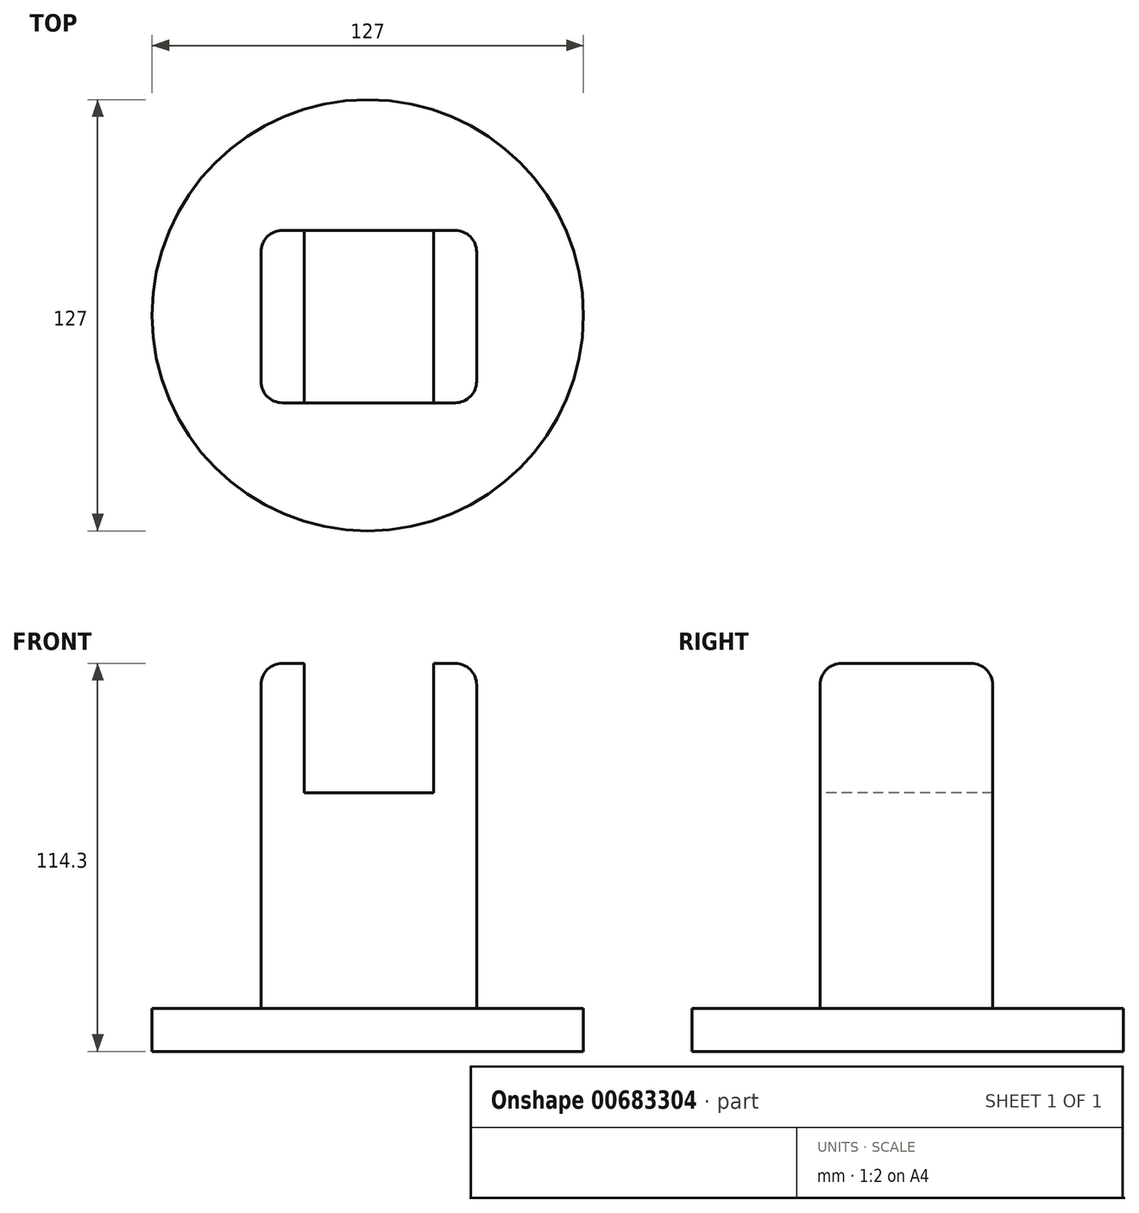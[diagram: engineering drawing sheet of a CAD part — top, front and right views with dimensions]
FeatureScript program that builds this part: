
annotation { "Feature Type Name" : "Feature", "Feature Type Description" : "" }
export const myFeature = defineFeature(function(context is Context, id is Id, definition is map)
    precondition{}
    {
        {
            var Q0;
            Q0=qCreatedBy(makeId("Top.planeOp"),FACE);
            var sketch = newSketch(context, id + "F0", { "sketchPlane" : qUnion([Q0])});
            skLineSegment(sketch, "E0.bottom", {"start": v(-125.08, 16.31) * mm, "end": v(-74.28, 16.31) * mm});
            skLineSegment(sketch, "E0.top", {"start": v(-125.08, -34.49) * mm, "end": v(-74.28, -34.49) * mm});
            skLineSegment(sketch, "E0.left", {"start": v(-131.43, 9.96) * mm, "end": v(-131.43, -28.14) * mm});
            skLineSegment(sketch, "E0.right", {"start": v(-67.93, 9.96) * mm, "end": v(-67.93, -28.14) * mm});
            skPoint(sketch, "E1.visualSharp", {"position": v(-131.43, -34.49) * mm});
            skArc(sketch, "E1.filletArc", {"start": v(-131.43, -28.14) * mm, "mid": v(-129.57, -32.63) * mm, "end": v(-125.08, -34.49) * mm});
            skPoint(sketch, "E2.visualSharp", {"position": v(-131.43, 16.31) * mm});
            skArc(sketch, "E2.filletArc", {"start": v(-125.08, 16.31) * mm, "mid": v(-129.57, 14.45) * mm, "end": v(-131.43, 9.96) * mm});
            skPoint(sketch, "E3.visualSharp", {"position": v(-67.93, -34.49) * mm});
            skArc(sketch, "E3.filletArc", {"start": v(-74.28, -34.49) * mm, "mid": v(-69.79, -32.63) * mm, "end": v(-67.93, -28.14) * mm});
            skPoint(sketch, "E4.visualSharp", {"position": v(-67.93, 16.31) * mm});
            skArc(sketch, "E4.filletArc", {"start": v(-67.93, 9.96) * mm, "mid": v(-69.79, 14.45) * mm, "end": v(-74.28, 16.31) * mm});
            skSolve(sketch);
        }
        {
            var Q0;
            Q0=makeQuery(id+"F0.imprint","IMPRINT",FACE,{"disambiguationData":[TD([[makeQuery(id+"F0.imprint","IMPRINT",EDGE,{"derivedFrom":sQuery(id+"F0.wireOp",EDGE,"E0.bottom")}),-1.0]])]});
            extrude(context, id + "F1", {"entities" : qUnion([Q0]), "depth" : 76.2 * mm, "offsetDistance" : 25.4 * mm});
        }
        {
            var Q0;
            Q0=qCreatedBy(makeId("Top.planeOp"),FACE);
            var sketch = newSketch(context, id + "F2", { "sketchPlane" : qUnion([Q0])});
            skCircle(sketch, "E5", {"center": v(-99.98, -8.68) * mm, "radius": 63.5 * mm});
            skSolve(sketch);
        }
        {
            var Q0;
            Q0=makeQuery(id+"F2.imprint","IMPRINT",FACE,{"disambiguationData":[TD([[makeQuery(id+"F2.imprint","IMPRINT",EDGE,{"derivedFrom":sQuery(id+"F2.wireOp",EDGE,"E5")}),1.0]])]});
            extrude(context, id + "F3", {"entities" : qUnion([Q0]), "operationType" : NewBodyOperationType.ADD, "depth" : 12.7 * mm, "offsetDistance" : 25.4 * mm});
        }
        {
            var Q0;
            Q0=makeQuery(id+"F1.opExtrude","CAP_FACE",FACE,{"disambiguationData":[OSD([sQuery(id+"F0.wireOp",EDGE,"E0.bottom"),sQuery(id+"F0.wireOp",EDGE,"E0.top"),sQuery(id+"F0.wireOp",EDGE,"E0.left"),sQuery(id+"F0.wireOp",EDGE,"E0.right"),sQuery(id+"F0.wireOp",EDGE,"E1.filletArc"),sQuery(id+"F0.wireOp",EDGE,"E2.filletArc"),sQuery(id+"F0.wireOp",EDGE,"E3.filletArc"),sQuery(id+"F0.wireOp",EDGE,"E4.filletArc")])],"isStart":false});
            var sketch = newSketch(context, id + "F4", { "sketchPlane" : qUnion([Q0])});
            skSolve(sketch);
        }
        {
            var Q0;
            Q0=makeQuery(id+"F1.opExtrude","SWEPT_FACE",FACE,{"disambiguationData":[OSD([sQuery(id+"F0.wireOp",EDGE,"E0.left")])]});
            var sketch = newSketch(context, id + "F5", { "sketchPlane" : qUnion([Q0])});
            skLineSegment(sketch, "E6.bottom", {"start": v(-9.96, 76.2) * mm, "end": v(28.14, 76.2) * mm});
            skLineSegment(sketch, "E6.top", {"start": v(-9.96, 114.3) * mm, "end": v(28.14, 114.3) * mm});
            skLineSegment(sketch, "E6.left", {"start": v(-9.96, 76.2) * mm, "end": v(-9.96, 114.3) * mm});
            skLineSegment(sketch, "E6.right", {"start": v(28.14, 76.2) * mm, "end": v(28.14, 114.3) * mm});
            skPoint(sketch, "E7.oppositeSnap0", {"position": v(-9.96, 95.25) * mm});
            skLineSegment(sketch, "E7.left", {"start": v(-9.96, 95.25) * mm, "end": v(-9.96, 95.25) * mm});
            skSolve(sketch);
        }
        {
            var Q0;
            Q0 = qSketchRegion(id + "F4", true);
            var Q1;
            Q1=makeQuery(id+"F5.imprint","IMPRINT",FACE,{"disambiguationData":[TD([[makeQuery(id+"F5.imprint","IMPRINT",EDGE,{"derivedFrom":sQuery(id+"F5.wireOp",EDGE,"E6.bottom")}),1.0]])]});
            var Q2;
            Q2=makeQuery(id+"F5.imprint","IMPRINT",FACE,{"disambiguationData":[TD([[makeQuery(id+"F5.imprint","IMPRINT",EDGE,{"derivedFrom":sQuery(id+"F5.wireOp",EDGE,"E6.bottom")}),-1.0]])]});
            extrude(context, id + "F6", {"entities" : qUnion([Q0, Q1, Q2]), "operationType" : NewBodyOperationType.ADD, "oppositeDirection" : true, "depth" : 12.7 * mm, "offsetDistance" : 25.4 * mm});
        }
        {
            var Q0;
            Q0=makeQuery(id+"F6.opExtrude","SWEPT_FACE",FACE,{"disambiguationData":[OSD([sQuery(id+"F5.wireOp",EDGE,"E6.left")])]});
            extrude(context, id + "F7", {"entities" : qUnion([Q0]), "operationType" : NewBodyOperationType.ADD, "depth" : 6.35 * mm, "offsetDistance" : 25.4 * mm});
        }
        {
            var Q0;
            Q0=makeQuery(id+"F6.opExtrude","SWEPT_FACE",FACE,{"disambiguationData":[OSD([sQuery(id+"F5.wireOp",EDGE,"E6.right")])]});
            extrude(context, id + "F8", {"entities" : qUnion([Q0]), "operationType" : NewBodyOperationType.ADD, "depth" : 6.35 * mm, "offsetDistance" : 25.4 * mm});
        }
        {
            var Q0;
            {var subQ0=sQuery(id+"F5.wireOp",EDGE,"E6.right");Q0=makeQuery(id+"F8.opExtrude","CAP_EDGE",EDGE,{"disambiguationData":[OSD([subQ0]),TDD([makeQuery(id+"F6.opExtrude","CAP_EDGE",EDGE,{"disambiguationData":[OSD([subQ0])],"isStart":true})])],"isStart":false});}
            var Q1;
            {var subQ0=sQuery(id+"F5.wireOp",EDGE,"E6.left");Q1=makeQuery(id+"F7.opExtrude","CAP_EDGE",EDGE,{"disambiguationData":[OSD([subQ0]),TDD([makeQuery(id+"F6.opExtrude","CAP_EDGE",EDGE,{"disambiguationData":[OSD([subQ0])],"isStart":true})])],"isStart":false});}
            fillet(context, id + "F9", {"entities" : qUnion([Q0, Q1]), "radius" : 6.35 * mm, "tangentPropagation" : true, "allowEdgeOverflow" : false});
        }
        {
            var Q0;
            Q0=makeQuery(id+"F1.opExtrude","SWEPT_FACE",FACE,{"disambiguationData":[OSD([sQuery(id+"F0.wireOp",EDGE,"E0.right")])]});
            var sketch = newSketch(context, id + "F10", { "sketchPlane" : qUnion([Q0])});
            skLineSegment(sketch, "E8.bottom", {"start": v(-28.14, 76.2) * mm, "end": v(9.96, 76.2) * mm});
            skLineSegment(sketch, "E8.top", {"start": v(-28.14, 114.3) * mm, "end": v(9.96, 114.3) * mm});
            skLineSegment(sketch, "E8.left", {"start": v(-28.14, 76.2) * mm, "end": v(-28.14, 114.3) * mm});
            skLineSegment(sketch, "E8.right", {"start": v(9.96, 76.2) * mm, "end": v(9.96, 114.3) * mm});
            skSolve(sketch);
        }
        {
            var Q0;
            Q0=makeQuery(id+"F10.imprint","IMPRINT",FACE,{"disambiguationData":[TD([[makeQuery(id+"F10.imprint","IMPRINT",EDGE,{"derivedFrom":sQuery(id+"F10.wireOp",EDGE,"E8.bottom")}),-1.0]])]});
            extrude(context, id + "F11", {"entities" : qUnion([Q0]), "operationType" : NewBodyOperationType.ADD, "oppositeDirection" : true, "depth" : 12.7 * mm, "offsetDistance" : 25.4 * mm});
        }
        {
            var Q0;
            Q0=makeQuery(id+"F11.opExtrude","SWEPT_FACE",FACE,{"disambiguationData":[OSD([sQuery(id+"F10.wireOp",EDGE,"E8.right")])]});
            extrude(context, id + "F12", {"entities" : qUnion([Q0]), "operationType" : NewBodyOperationType.ADD, "depth" : 6.35 * mm, "offsetDistance" : 25.4 * mm});
        }
        {
            var Q0;
            Q0=makeQuery(id+"F11.opExtrude","SWEPT_FACE",FACE,{"disambiguationData":[OSD([sQuery(id+"F10.wireOp",EDGE,"E8.left")])]});
            extrude(context, id + "F13", {"entities" : qUnion([Q0]), "operationType" : NewBodyOperationType.ADD, "depth" : 6.35 * mm, "offsetDistance" : 25.4 * mm});
        }
        {
            var Q0;
            {var subQ0=sQuery(id+"F5.wireOp",EDGE,"E6.right");var subQ1=sQuery(id+"F0.wireOp",EDGE,"E1.filletArc");var subQ2=sQuery(id+"F0.wireOp",EDGE,"E0.left");Q0=makeQuery(id+"F8.opExtrude","CAP_EDGE",EDGE,{"disambiguationData":[OSD([subQ2,subQ1,subQ0]),TDD([makeQuery(id+"F6.opExtrude","CAP_EDGE",EDGE,{"disambiguationData":[OSD([subQ2,subQ1,subQ0])],"isStart":true})])],"isStart":false});}
            var Q1;
            {var subQ0=sQuery(id+"F10.wireOp",EDGE,"E8.left");Q1=makeQuery(id+"F13.opExtrude","CAP_EDGE",EDGE,{"disambiguationData":[OSD([subQ0]),TDD([makeQuery(id+"F11.opExtrude","CAP_EDGE",EDGE,{"disambiguationData":[OSD([subQ0])],"isStart":true})])],"isStart":false});}
            var Q2;
            {var subQ0=sQuery(id+"F10.wireOp",EDGE,"E8.right");Q2=makeQuery(id+"F12.opExtrude","CAP_EDGE",EDGE,{"disambiguationData":[OSD([subQ0]),TDD([makeQuery(id+"F11.opExtrude","CAP_EDGE",EDGE,{"disambiguationData":[OSD([subQ0])],"isStart":true})])],"isStart":false});}
            var Q3;
            {var subQ0=sQuery(id+"F10.wireOp",EDGE,"E8.left");var subQ1=sQuery(id+"F10.wireOp",EDGE,"E8.top");var subQ2=sQuery(id+"F10.wireOp",EDGE,"E8.right");Q3=makeQuery(id+"F13.boolean.opBoolean","MERGE",EDGE,{"derivedFrom":[makeQuery(id+"F12.boolean.opBoolean","MERGE",EDGE,{"derivedFrom":[makeQuery(id+"F11.opExtrude","CAP_EDGE",EDGE,{"disambiguationData":[OSD([subQ1])],"isStart":true}),makeQuery(id+"F12.opExtrude","SWEPT_EDGE",EDGE,{"disambiguationData":[OSD([subQ1,subQ2]),TDD([makeQuery(id+"F11.opExtrude","CAP_VERTEX",VERTEX,{"disambiguationData":[OSD([subQ1,subQ2])],"isStart":true})])]})]}),makeQuery(id+"F13.opExtrude","SWEPT_EDGE",EDGE,{"disambiguationData":[OSD([subQ1,subQ0]),TDD([makeQuery(id+"F11.opExtrude","CAP_VERTEX",VERTEX,{"disambiguationData":[OSD([subQ1,subQ0])],"isStart":true})])]})]});}
            var Q4;
            Q4=makeQuery(id+"F13.opExtrude","CAP_EDGE",EDGE,{"disambiguationData":[OSD([sQuery(id+"F10.wireOp",EDGE,"E8.top"),sQuery(id+"F10.wireOp",EDGE,"E8.left")])],"isStart":false});
            var Q5;
            Q5=makeQuery(id+"F12.opExtrude","CAP_EDGE",EDGE,{"disambiguationData":[OSD([sQuery(id+"F10.wireOp",EDGE,"E8.top"),sQuery(id+"F10.wireOp",EDGE,"E8.right")])],"isStart":false});
            fillet(context, id + "F14", {"entities" : qUnion([Q0, Q1, Q2, Q3, Q4, Q5]), "radius" : 6.35 * mm, "tangentPropagation" : true, "allowEdgeOverflow" : false});
        }
    });
